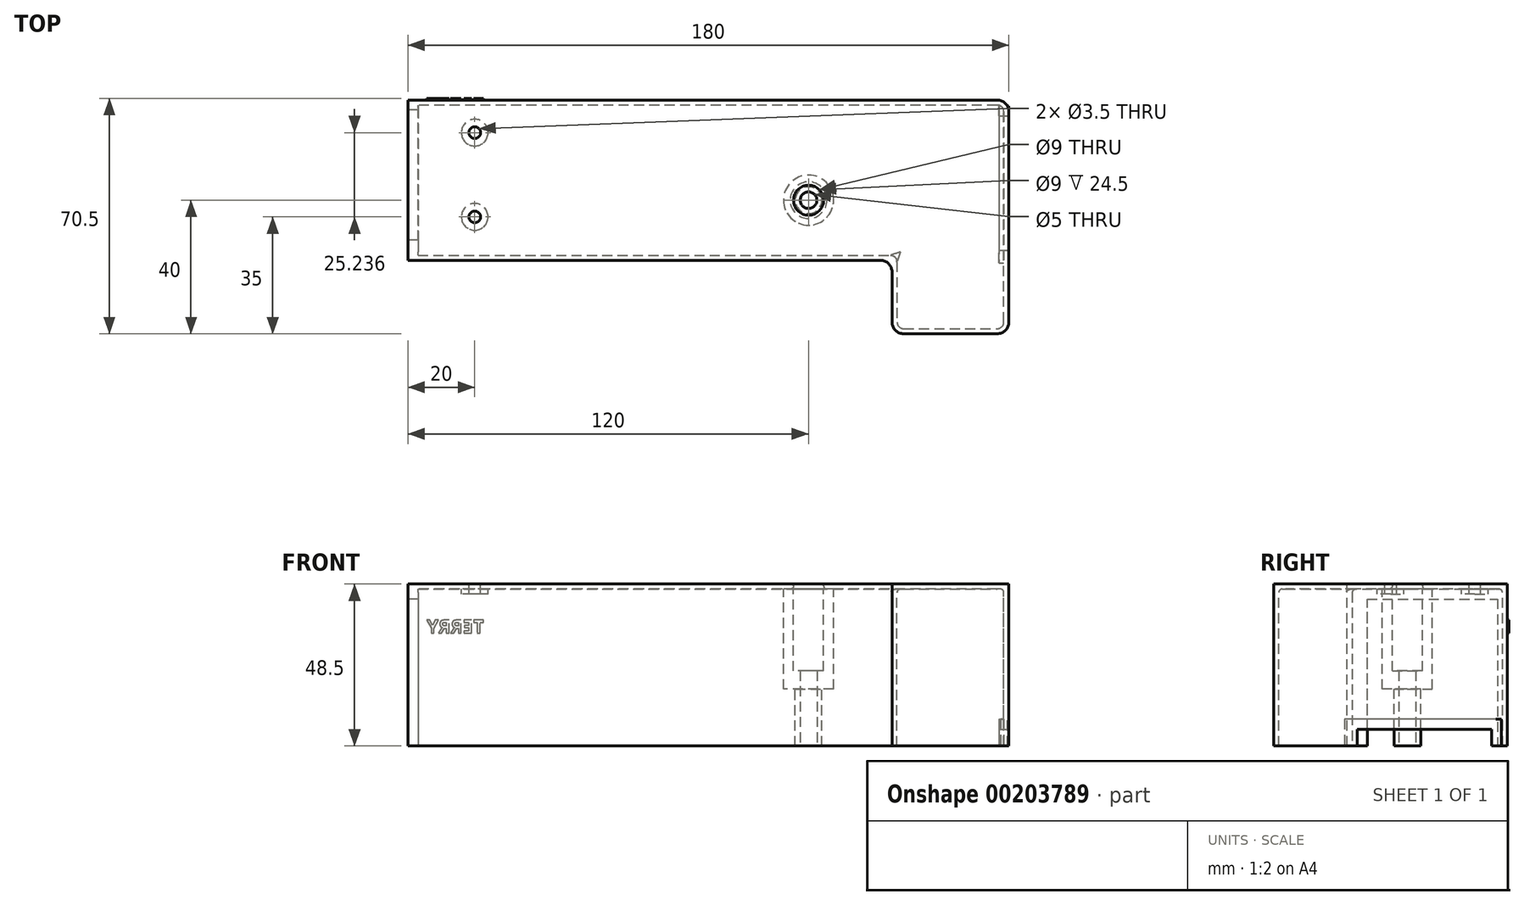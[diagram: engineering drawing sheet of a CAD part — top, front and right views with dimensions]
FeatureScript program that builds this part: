
annotation { "Feature Type Name" : "Feature", "Feature Type Description" : "" }
export const myFeature = defineFeature(function(context is Context, id is Id, definition is map)
    precondition{}
    {
        {
            var Q0;
            Q0=qCreatedBy(makeId("Top.planeOp"),FACE);
            var sketch = newSketch(context, id + "F0", { "sketchPlane" : qUnion([Q0])});
            skLineSegment(sketch, "E0", {"start": v(0, 0) * mm, "end": v(0, -22) * mm});
            skLineSegment(sketch, "E1", {"start": v(0, -22) * mm, "end": v(35, -22) * mm});
            skLineSegment(sketch, "E2", {"start": v(35, -22) * mm, "end": v(35, 48) * mm});
            skLineSegment(sketch, "E3", {"start": v(35, 48) * mm, "end": v(-145, 48) * mm});
            skLineSegment(sketch, "E4", {"start": v(-145, 48) * mm, "end": v(-145, 0) * mm});
            skLineSegment(sketch, "E5", {"start": v(-145, 0) * mm, "end": v(0, 0) * mm});
            skLineSegment(sketch, "E6", {"start": v(-145, 48) * mm, "end": v(-145, 18) * mm, "construction": true});
            skLineSegment(sketch, "E7", {"start": v(-145, 18) * mm, "end": v(-25, 18) * mm, "construction": true});
            skCircle(sketch, "E8", {"center": v(-25, 18) * mm, "radius": 2.25 * mm});
            skCircle(sketch, "E9", {"center": v(-25, 18) * mm, "radius": 4.5 * mm});
            skSolve(sketch);
        }
        {
            var Q0;
            Q0=makeQuery(id+"F0.imprint","IMPRINT",FACE,{"disambiguationData":[TD([[makeQuery(id+"F0.imprint","IMPRINT",EDGE,{"derivedFrom":sQuery(id+"F0.wireOp",EDGE,"E0")}),1.0]])]});
            var Q1;
            Q1=makeQuery(id+"F0.imprint","IMPRINT",FACE,{"disambiguationData":[TD([[makeQuery(id+"F0.imprint","IMPRINT",EDGE,{"derivedFrom":sQuery(id+"F0.wireOp",EDGE,"E8")}),1.0]])]});
            extrude(context, id + "F1", {"entities" : qUnion([Q0, Q1]), "oppositeDirection" : true, "depth" : 1.5 * mm});
        }
        {
            var Q0;
            Q0=makeQuery(id+"F1.opExtrude","CAP_FACE",FACE,{"disambiguationData":[OSD([sQuery(id+"F0.wireOp",EDGE,"E0"),sQuery(id+"F0.wireOp",EDGE,"E1"),sQuery(id+"F0.wireOp",EDGE,"E2"),sQuery(id+"F0.wireOp",EDGE,"E3"),sQuery(id+"F0.wireOp",EDGE,"E4"),sQuery(id+"F0.wireOp",EDGE,"E5")])],"isStart":false});
            var sketch = newSketch(context, id + "F2", { "sketchPlane" : qUnion([Q0])});
            skLineSegment(sketch, "E10", {"start": v(-145, 0) * mm, "end": v(0, 0) * mm});
            skLineSegment(sketch, "E11", {"start": v(0, 0) * mm, "end": v(0, 22) * mm});
            skLineSegment(sketch, "E12", {"start": v(0, 22) * mm, "end": v(35, 22) * mm});
            skLineSegment(sketch, "E13", {"start": v(35, 22) * mm, "end": v(35, -48) * mm});
            skLineSegment(sketch, "E14", {"start": v(35, -48) * mm, "end": v(-145, -48) * mm});
            skLineSegment(sketch, "E15", {"start": v(-145, -48) * mm, "end": v(-145, 0) * mm});
            skLineSegment(sketch, "E16.0", {"start": v(-143.5, -46.5) * mm, "end": v(-143.5, -1.5) * mm});
            skLineSegment(sketch, "E16.1", {"start": v(1.5, -1.5) * mm, "end": v(1.5, 20.5) * mm});
            skLineSegment(sketch, "E16.2", {"start": v(1.5, 20.5) * mm, "end": v(33.5, 20.5) * mm});
            skLineSegment(sketch, "E16.3", {"start": v(-143.5, -1.5) * mm, "end": v(1.5, -1.5) * mm});
            skLineSegment(sketch, "E16.4", {"start": v(33.5, 20.5) * mm, "end": v(33.5, -46.5) * mm});
            skLineSegment(sketch, "E16.5", {"start": v(33.5, -46.5) * mm, "end": v(-143.5, -46.5) * mm});
            skLineSegment(sketch, "E17", {"start": v(-145, 0) * mm, "end": v(-145, -18) * mm, "construction": true});
            skLineSegment(sketch, "E18", {"start": v(-145, -18) * mm, "end": v(-25, -18) * mm, "construction": true});
            skCircle(sketch, "E19", {"center": v(-25, -18) * mm, "radius": 4 * mm});
            skSolve(sketch);
        }
        {
            var Q0;
            Q0=makeQuery(id+"F2.imprint","IMPRINT",FACE,{"disambiguationData":[TD([[makeQuery(id+"F2.imprint","IMPRINT",EDGE,{"derivedFrom":sQuery(id+"F2.wireOp",EDGE,"E10")}),-1.0]])]});
            var Q1;
            Q1=makeQuery(id+"F2.imprint","IMPRINT",FACE,{"disambiguationData":[TD([[makeQuery(id+"F2.imprint","IMPRINT",EDGE,{"derivedFrom":sQuery(id+"F2.wireOp",EDGE,"E19")}),1.0]])]});
            extrude(context, id + "F3", {"entities" : qUnion([Q0, Q1]), "operationType" : NewBodyOperationType.ADD, "depth" : 47 * mm});
        }
        {
            var Q0;
            Q0=makeQuery(id+"F3.opExtrude","CAP_FACE",FACE,{"disambiguationData":[OSD([sQuery(id+"F2.wireOp",EDGE,"E19")])],"isStart":false});
            var sketch = newSketch(context, id + "F4", { "sketchPlane" : qUnion([Q0])});
            skCircle(sketch, "E20", {"center": v(-25, -18) * mm, "radius": 2.25 * mm});
            skSolve(sketch);
        }
        {
            var Q0;
            Q0=makeQuery(id+"F4.imprint","IMPRINT",FACE,{"disambiguationData":[TD([[makeQuery(id+"F4.imprint","IMPRINT",EDGE,{"derivedFrom":sQuery(id+"F4.wireOp",EDGE,"E20")}),1.0]])]});
            extrude(context, id + "F5", {"entities" : qUnion([Q0]), "operationType" : NewBodyOperationType.REMOVE, "endBound" : BoundingType.UP_TO_NEXT, "oppositeDirection" : true, "depth" : 25 * mm});
        }
        {
            var Q0;
            Q0=makeQuery(id+"F3.boolean.opBoolean","MERGE",FACE,{"derivedFrom":[makeQuery(id+"F1.opExtrude","SWEPT_FACE",FACE,{"disambiguationData":[OSD([sQuery(id+"F0.wireOp",EDGE,"E2")])]}),makeQuery(id+"F3.opExtrude","SWEPT_FACE",FACE,{"disambiguationData":[OSD([sQuery(id+"F2.wireOp",EDGE,"E13")])]})]});
            var sketch = newSketch(context, id + "F6", { "sketchPlane" : qUnion([Q0])});
            skLineSegment(sketch, "E21", {"start": v(48, -48.5) * mm, "end": v(45, -48.5) * mm, "construction": true});
            skLineSegment(sketch, "E22", {"start": v(45, -48.5) * mm, "end": v(45, -43.5) * mm});
            skLineSegment(sketch, "E23", {"start": v(45, -43.5) * mm, "end": v(3, -43.5) * mm});
            skLineSegment(sketch, "E24", {"start": v(3, -43.5) * mm, "end": v(3, -48.5) * mm});
            skLineSegment(sketch, "E25", {"start": v(3, -48.5) * mm, "end": v(45, -48.5) * mm});
            skLineSegment(sketch, "E26", {"start": v(3, -48.5) * mm, "end": v(0, -48.5) * mm});
            skLineSegment(sketch, "E27", {"start": v(0, -48.5) * mm, "end": v(0, -40.5) * mm});
            skLineSegment(sketch, "E28", {"start": v(0, -40.5) * mm, "end": v(48, -40.5) * mm});
            skLineSegment(sketch, "E29", {"start": v(48, -40.5) * mm, "end": v(48, -48.5) * mm});
            skSolve(sketch);
        }
        {
            var Q0;
            Q0=makeQuery(id+"F6.imprint","IMPRINT",FACE,{"disambiguationData":[TD([[makeQuery(id+"F6.imprint","IMPRINT",EDGE,{"derivedFrom":sQuery(id+"F6.wireOp",EDGE,"E22")}),1.0]])]});
            extrude(context, id + "F7", {"entities" : qUnion([Q0]), "operationType" : NewBodyOperationType.REMOVE, "endBound" : BoundingType.UP_TO_NEXT, "oppositeDirection" : true, "depth" : 25 * mm});
        }
        {
            var Q0;
            Q0=makeQuery(id+"F3.boolean.opBoolean","MERGE",FACE,{"derivedFrom":[makeQuery(id+"F1.opExtrude","SWEPT_FACE",FACE,{"disambiguationData":[OSD([sQuery(id+"F0.wireOp",EDGE,"E4")])]}),makeQuery(id+"F3.opExtrude","SWEPT_FACE",FACE,{"disambiguationData":[OSD([sQuery(id+"F2.wireOp",EDGE,"E15")])]})]});
            var sketch = newSketch(context, id + "F8", { "sketchPlane" : qUnion([Q0])});
            skLineSegment(sketch, "E30", {"start": v(-48, -48.5) * mm, "end": v(-45, -48.5) * mm, "construction": true});
            skLineSegment(sketch, "E31", {"start": v(-45, -48.5) * mm, "end": v(-6, -48.5) * mm});
            skLineSegment(sketch, "E32", {"start": v(-6, -48.5) * mm, "end": v(-6, -4.5) * mm});
            skLineSegment(sketch, "E33", {"start": v(-6, -4.5) * mm, "end": v(-45, -4.5) * mm});
            skLineSegment(sketch, "E34", {"start": v(-45, -4.5) * mm, "end": v(-45, -48.5) * mm});
            skLineSegment(sketch, "E35", {"start": v(-45, -48.5) * mm, "end": v(-48, -48.5) * mm});
            skLineSegment(sketch, "E36", {"start": v(-48, 0) * mm, "end": v(0, 0) * mm});
            skLineSegment(sketch, "E37", {"start": v(0, 0) * mm, "end": v(0, -48.5) * mm});
            skLineSegment(sketch, "E38", {"start": v(0, -48.5) * mm, "end": v(-6, -48.5) * mm});
            skSolve(sketch);
        }
        {
            var Q0;
            Q0=makeQuery(id+"F8.imprint","IMPRINT",FACE,{"disambiguationData":[TD([[makeQuery(id+"F8.imprint","IMPRINT",EDGE,{"derivedFrom":sQuery(id+"F8.wireOp",EDGE,"E31")}),1.0]])]});
            extrude(context, id + "F9", {"entities" : qUnion([Q0]), "operationType" : NewBodyOperationType.REMOVE, "endBound" : BoundingType.UP_TO_NEXT, "oppositeDirection" : true, "depth" : 25 * mm});
        }
        {
            var Q0;
            Q0=makeQuery(id+"F9.boolean.opBoolean","MERGE",FACE,{"derivedFrom":[makeQuery(id+"F1.opExtrude","CAP_FACE",FACE,{"disambiguationData":[OSD([sQuery(id+"F0.wireOp",EDGE,"E0"),sQuery(id+"F0.wireOp",EDGE,"E1"),sQuery(id+"F0.wireOp",EDGE,"E2"),sQuery(id+"F0.wireOp",EDGE,"E3"),sQuery(id+"F0.wireOp",EDGE,"E4"),sQuery(id+"F0.wireOp",EDGE,"E5")])],"isStart":false}),makeQuery(id+"F9.opExtrude","SWEPT_FACE",FACE,{"disambiguationData":[OSD([sQuery(id+"F8.wireOp",EDGE,"E33")])]})]});
            fillet(context, id + "F10", {"entities" : qUnion([Q0]), "radius" : 1 * mm, "tangentPropagation" : true, "allowEdgeOverflow" : false});
        }
        {
            var Q0;
            Q0=makeQuery(id+"F3.opExtrude","SWEPT_EDGE",EDGE,{"disambiguationData":[OSD([sQuery(id+"F2.wireOp",EDGE,"E16.4"),sQuery(id+"F2.wireOp",EDGE,"E16.5")])]});
            var Q1;
            Q1=makeQuery(id+"F3.opExtrude","SWEPT_EDGE",EDGE,{"disambiguationData":[OSD([sQuery(id+"F2.wireOp",EDGE,"E16.1"),sQuery(id+"F2.wireOp",EDGE,"E16.3")])]});
            var Q2;
            Q2=makeQuery(id+"F3.opExtrude","SWEPT_EDGE",EDGE,{"disambiguationData":[OSD([sQuery(id+"F2.wireOp",EDGE,"E16.1"),sQuery(id+"F2.wireOp",EDGE,"E16.2")])]});
            var Q3;
            Q3=makeQuery(id+"F3.opExtrude","SWEPT_EDGE",EDGE,{"disambiguationData":[OSD([sQuery(id+"F2.wireOp",EDGE,"E16.2"),sQuery(id+"F2.wireOp",EDGE,"E16.4")])]});
            fillet(context, id + "F11", {"entities" : qUnion([Q0, Q1, Q2, Q3]), "radius" : 2 * mm, "tangentPropagation" : true, "allowEdgeOverflow" : false});
        }
        {
            var Q0;
            Q0=makeQuery(id+"F3.boolean.opBoolean","MERGE",EDGE,{"derivedFrom":[makeQuery(id+"F1.opExtrude","SWEPT_EDGE",EDGE,{"disambiguationData":[OSD([sQuery(id+"F0.wireOp",EDGE,"E0"),sQuery(id+"F0.wireOp",EDGE,"E5")])]}),makeQuery(id+"F3.opExtrude","SWEPT_EDGE",EDGE,{"disambiguationData":[OSD([sQuery(id+"F2.wireOp",EDGE,"E10"),sQuery(id+"F2.wireOp",EDGE,"E11")])]})]});
            var Q1;
            Q1=makeQuery(id+"F3.boolean.opBoolean","MERGE",EDGE,{"derivedFrom":[makeQuery(id+"F1.opExtrude","SWEPT_EDGE",EDGE,{"disambiguationData":[OSD([sQuery(id+"F0.wireOp",EDGE,"E0"),sQuery(id+"F0.wireOp",EDGE,"E1")])]}),makeQuery(id+"F3.opExtrude","SWEPT_EDGE",EDGE,{"disambiguationData":[OSD([sQuery(id+"F2.wireOp",EDGE,"E11"),sQuery(id+"F2.wireOp",EDGE,"E12")])]})]});
            var Q2;
            Q2=makeQuery(id+"F3.boolean.opBoolean","MERGE",EDGE,{"derivedFrom":[makeQuery(id+"F1.opExtrude","SWEPT_EDGE",EDGE,{"disambiguationData":[OSD([sQuery(id+"F0.wireOp",EDGE,"E1"),sQuery(id+"F0.wireOp",EDGE,"E2")])]}),makeQuery(id+"F3.opExtrude","SWEPT_EDGE",EDGE,{"disambiguationData":[OSD([sQuery(id+"F2.wireOp",EDGE,"E12"),sQuery(id+"F2.wireOp",EDGE,"E13")])]})]});
            var Q3;
            Q3=makeQuery(id+"F3.boolean.opBoolean","MERGE",EDGE,{"derivedFrom":[makeQuery(id+"F1.opExtrude","SWEPT_EDGE",EDGE,{"disambiguationData":[OSD([sQuery(id+"F0.wireOp",EDGE,"E2"),sQuery(id+"F0.wireOp",EDGE,"E3")])]}),makeQuery(id+"F3.opExtrude","SWEPT_EDGE",EDGE,{"disambiguationData":[OSD([sQuery(id+"F2.wireOp",EDGE,"E13"),sQuery(id+"F2.wireOp",EDGE,"E14")])]})]});
            fillet(context, id + "F12", {"entities" : qUnion([Q0, Q1, Q2, Q3]), "radius" : 3.5 * mm, "tangentPropagation" : true, "allowEdgeOverflow" : false});
        }
        {
            var Q0;
            Q0=makeQuery(id+"F3.boolean.opBoolean","MERGE",FACE,{"derivedFrom":[makeQuery(id+"F1.opExtrude","SWEPT_FACE",FACE,{"disambiguationData":[OSD([sQuery(id+"F0.wireOp",EDGE,"E3")])]}),makeQuery(id+"F3.opExtrude","SWEPT_FACE",FACE,{"disambiguationData":[OSD([sQuery(id+"F2.wireOp",EDGE,"E14")])]})]});
            var sketch = newSketch(context, id + "F13", { "sketchPlane" : qUnion([Q0])});
            skText(sketch, "E39", { "text": "TERRY", "fontName": "OpenSans-Bold.ttf"});
            const initialGuessF13  = {"E39": [0.12223, -0.01474, 1, 0, 0.004]};
            skSetInitialGuess(sketch, initialGuessF13);
            skSolve(sketch);
        }
        {
            var Q0;
            Q0 = qSketchRegion(id + "F13", true);
            extrude(context, id + "F14", {"entities" : qUnion([Q0]), "operationType" : NewBodyOperationType.ADD, "depth" : 0.5 * mm});
        }
        {
            var Q0;
            Q0=makeQuery(id+"F3.boolean.opBoolean","MERGE",FACE,{"derivedFrom":[makeQuery(id+"F1.opExtrude","SWEPT_FACE",FACE,{"disambiguationData":[OSD([sQuery(id+"F0.wireOp",EDGE,"E4")])]}),makeQuery(id+"F3.opExtrude","SWEPT_FACE",FACE,{"disambiguationData":[OSD([sQuery(id+"F2.wireOp",EDGE,"E15")])]})]});
            extrude(context, id + "F15", {"entities" : qUnion([Q0]), "operationType" : NewBodyOperationType.ADD, "oppositeDirection" : true, "depth" : 3 * mm});
        }
        {
            var Q0;
            Q0=makeQuery(id+"F3.boolean.opBoolean","MERGE",FACE,{"derivedFrom":[makeQuery(id+"F1.opExtrude","SWEPT_FACE",FACE,{"disambiguationData":[OSD([sQuery(id+"F0.wireOp",EDGE,"E2")])]}),makeQuery(id+"F3.opExtrude","SWEPT_FACE",FACE,{"disambiguationData":[OSD([sQuery(id+"F2.wireOp",EDGE,"E13")])]})]});
            var sketch = newSketch(context, id + "F16", { "sketchPlane" : qUnion([Q0])});
            skLineSegment(sketch, "E40", {"start": v(3, -48.5) * mm, "end": v(3, -43.5) * mm});
            skLineSegment(sketch, "E41", {"start": v(3, -43.5) * mm, "end": v(43.23, -43.5) * mm});
            skLineSegment(sketch, "E42", {"start": v(43.23, -43.5) * mm, "end": v(43.23, -48.5) * mm});
            skLineSegment(sketch, "E43", {"start": v(43.23, -48.5) * mm, "end": v(46.23, -48.5) * mm});
            skLineSegment(sketch, "E44", {"start": v(46.23, -48.5) * mm, "end": v(46.23, -40.5) * mm});
            skLineSegment(sketch, "E45", {"start": v(46.23, -40.5) * mm, "end": v(-0.77, -40.5) * mm});
            skLineSegment(sketch, "E46", {"start": v(-0.77, -40.5) * mm, "end": v(-0.77, -48.5) * mm});
            skLineSegment(sketch, "E47", {"start": v(-0.77, -48.5) * mm, "end": v(3, -48.5) * mm});
            skSolve(sketch);
        }
        {
            var Q0;
            Q0=makeQuery(id+"F16.imprint","IMPRINT",FACE,{"disambiguationData":[TD([[makeQuery(id+"F16.imprint","IMPRINT",EDGE,{"derivedFrom":sQuery(id+"F16.wireOp",EDGE,"E40")}),-1.0]])]});
            var Q1;
            {var subQ6=sQuery(id+"F16.wireOp",EDGE,"E42");Q1=makeQuery(id+"F16.imprint","IMPRINT",FACE,{"disambiguationData":[TD([[makeQuery(id+"F16.imprint","IMPRINT",EDGE,{"derivedFrom":subQ6}),1.0]])]});}
            extrude(context, id + "F17", {"entities" : qUnion([Q0, Q1]), "operationType" : NewBodyOperationType.ADD, "oppositeDirection" : true, "depth" : 3 * mm});
        }
        {
            var Q0;
            Q0=makeQuery(id+"F1.opExtrude","CAP_FACE",FACE,{"disambiguationData":[OSD([sQuery(id+"F0.wireOp",EDGE,"E0"),sQuery(id+"F0.wireOp",EDGE,"E1"),sQuery(id+"F0.wireOp",EDGE,"E2"),sQuery(id+"F0.wireOp",EDGE,"E3"),sQuery(id+"F0.wireOp",EDGE,"E4"),sQuery(id+"F0.wireOp",EDGE,"E5")])],"isStart":false});
            var sketch = newSketch(context, id + "F18", { "sketchPlane" : qUnion([Q0])});
            skCircle(sketch, "E48", {"center": v(-25, -18) * mm, "radius": 3.5 * mm});
            skCircle(sketch, "E49", {"center": v(-25, -18) * mm, "radius": 7.5 * mm});
            skSolve(sketch);
        }
        {
            var Q0;
            Q0=makeQuery(id+"F18.imprint","IMPRINT",FACE,{"disambiguationData":[TD([[makeQuery(id+"F18.imprint","IMPRINT",EDGE,{"derivedFrom":sQuery(id+"F18.wireOp",EDGE,"E48")}),-1.0]])]});
            var Q1;
            Q1=makeQuery(id+"F18.imprint","IMPRINT",FACE,{"disambiguationData":[TD([[makeQuery(id+"F18.imprint","IMPRINT",EDGE,{"derivedFrom":sQuery(id+"F18.wireOp",EDGE,"E49")}),1.0]])]});
            extrude(context, id + "F19", {"entities" : qUnion([Q0, Q1]), "operationType" : NewBodyOperationType.ADD, "depth" : 30 * mm});
        }
        {
            var Q0;
            Q0=makeQuery(id+"F0.imprint","IMPRINT",FACE,{"disambiguationData":[TD([[makeQuery(id+"F0.imprint","IMPRINT",EDGE,{"derivedFrom":sQuery(id+"F0.wireOp",EDGE,"E8")}),-1.0]])]});
            var Q1;
            Q1=makeQuery(id+"F0.imprint","IMPRINT",FACE,{"disambiguationData":[TD([[makeQuery(id+"F0.imprint","IMPRINT",EDGE,{"derivedFrom":sQuery(id+"F0.wireOp",EDGE,"E8")}),1.0]])]});
            extrude(context, id + "F20", {"entities" : qUnion([Q0, Q1]), "operationType" : NewBodyOperationType.REMOVE, "oppositeDirection" : true, "depth" : 26 * mm});
        }
        {
            var Q0;
            Q0=makeQuery(id+"F3.opExtrude","CAP_FACE",FACE,{"disambiguationData":[OSD([sQuery(id+"F2.wireOp",EDGE,"E19")])],"isStart":false});
            var sketch = newSketch(context, id + "F21", { "sketchPlane" : qUnion([Q0])});
            skCircle(sketch, "E50", {"center": v(-25, -18) * mm, "radius": 2.5 * mm});
            skSolve(sketch);
        }
        {
            var Q0;
            Q0=makeQuery(id+"F21.imprint","IMPRINT",FACE,{"disambiguationData":[TD([[makeQuery(id+"F21.imprint","IMPRINT",EDGE,{"derivedFrom":sQuery(id+"F21.wireOp",EDGE,"E50")}),1.0]])]});
            extrude(context, id + "F22", {"entities" : qUnion([Q0]), "operationType" : NewBodyOperationType.REMOVE, "endBound" : BoundingType.THROUGH_ALL, "oppositeDirection" : true, "depth" : 25 * mm});
        }
        {
            var Q0;
            Q0=makeQuery(id+"F1.opExtrude","CAP_FACE",FACE,{"disambiguationData":[OSD([sQuery(id+"F0.wireOp",EDGE,"E0"),sQuery(id+"F0.wireOp",EDGE,"E1"),sQuery(id+"F0.wireOp",EDGE,"E2"),sQuery(id+"F0.wireOp",EDGE,"E3"),sQuery(id+"F0.wireOp",EDGE,"E4"),sQuery(id+"F0.wireOp",EDGE,"E5"),sQuery(id+"F0.wireOp",EDGE,"E9")])],"isStart":false});
            var sketch = newSketch(context, id + "F23", { "sketchPlane" : qUnion([Q0])});
            skLineSegment(sketch, "E51", {"start": v(-142, -2.5) * mm, "end": v(-142, -13) * mm, "construction": true});
            skLineSegment(sketch, "E52", {"start": v(-142, -13) * mm, "end": v(-125, -13) * mm, "construction": true});
            skLineSegment(sketch, "E53", {"start": v(-125, -13) * mm, "end": v(-125, -38.24) * mm, "construction": true});
            skCircle(sketch, "E54", {"center": v(-125, -13) * mm, "radius": 1.75 * mm});
            skCircle(sketch, "E55", {"center": v(-125, -38.24) * mm, "radius": 1.75 * mm});
            skCircle(sketch, "E56", {"center": v(-125, -13) * mm, "radius": 4 * mm});
            skCircle(sketch, "E57", {"center": v(-125, -38.24) * mm, "radius": 4 * mm});
            skSolve(sketch);
        }
        {
            var Q0;
            Q0=makeQuery(id+"F23.imprint","IMPRINT",FACE,{"disambiguationData":[TD([[makeQuery(id+"F23.imprint","IMPRINT",EDGE,{"derivedFrom":sQuery(id+"F23.wireOp",EDGE,"E54")}),-1.0]])]});
            var Q1;
            Q1=makeQuery(id+"F23.imprint","IMPRINT",FACE,{"disambiguationData":[TD([[makeQuery(id+"F23.imprint","IMPRINT",EDGE,{"derivedFrom":sQuery(id+"F23.wireOp",EDGE,"E55")}),-1.0]])]});
            extrude(context, id + "F24", {"entities" : qUnion([Q0, Q1]), "operationType" : NewBodyOperationType.ADD, "depth" : 1.5 * mm});
        }
        {
            var Q0;
            Q0=makeQuery(id+"F24.boolean.opBoolean","SPLIT",FACE,{"disambiguationData":[TD([makeQuery(id+"F24.opExtrude","SWEPT_FACE",FACE,{"disambiguationData":[OSD([sQuery(id+"F23.wireOp",EDGE,"E54")])]})])],"derivedFrom":makeQuery(id+"F1.opExtrude","CAP_FACE",FACE,{"disambiguationData":[OSD([sQuery(id+"F0.wireOp",EDGE,"E0"),sQuery(id+"F0.wireOp",EDGE,"E1"),sQuery(id+"F0.wireOp",EDGE,"E2"),sQuery(id+"F0.wireOp",EDGE,"E3"),sQuery(id+"F0.wireOp",EDGE,"E4"),sQuery(id+"F0.wireOp",EDGE,"E5"),sQuery(id+"F0.wireOp",EDGE,"E9")])],"isStart":false})});
            var Q1;
            Q1=makeQuery(id+"F24.boolean.opBoolean","SPLIT",FACE,{"disambiguationData":[TD([makeQuery(id+"F24.opExtrude","SWEPT_FACE",FACE,{"disambiguationData":[OSD([sQuery(id+"F23.wireOp",EDGE,"E55")])]})])],"derivedFrom":makeQuery(id+"F1.opExtrude","CAP_FACE",FACE,{"disambiguationData":[OSD([sQuery(id+"F0.wireOp",EDGE,"E0"),sQuery(id+"F0.wireOp",EDGE,"E1"),sQuery(id+"F0.wireOp",EDGE,"E2"),sQuery(id+"F0.wireOp",EDGE,"E3"),sQuery(id+"F0.wireOp",EDGE,"E4"),sQuery(id+"F0.wireOp",EDGE,"E5"),sQuery(id+"F0.wireOp",EDGE,"E9")])],"isStart":false})});
            extrude(context, id + "F25", {"entities" : qUnion([Q0, Q1]), "operationType" : NewBodyOperationType.REMOVE, "endBound" : BoundingType.THROUGH_ALL, "oppositeDirection" : true, "depth" : 25 * mm});
        }
    });
